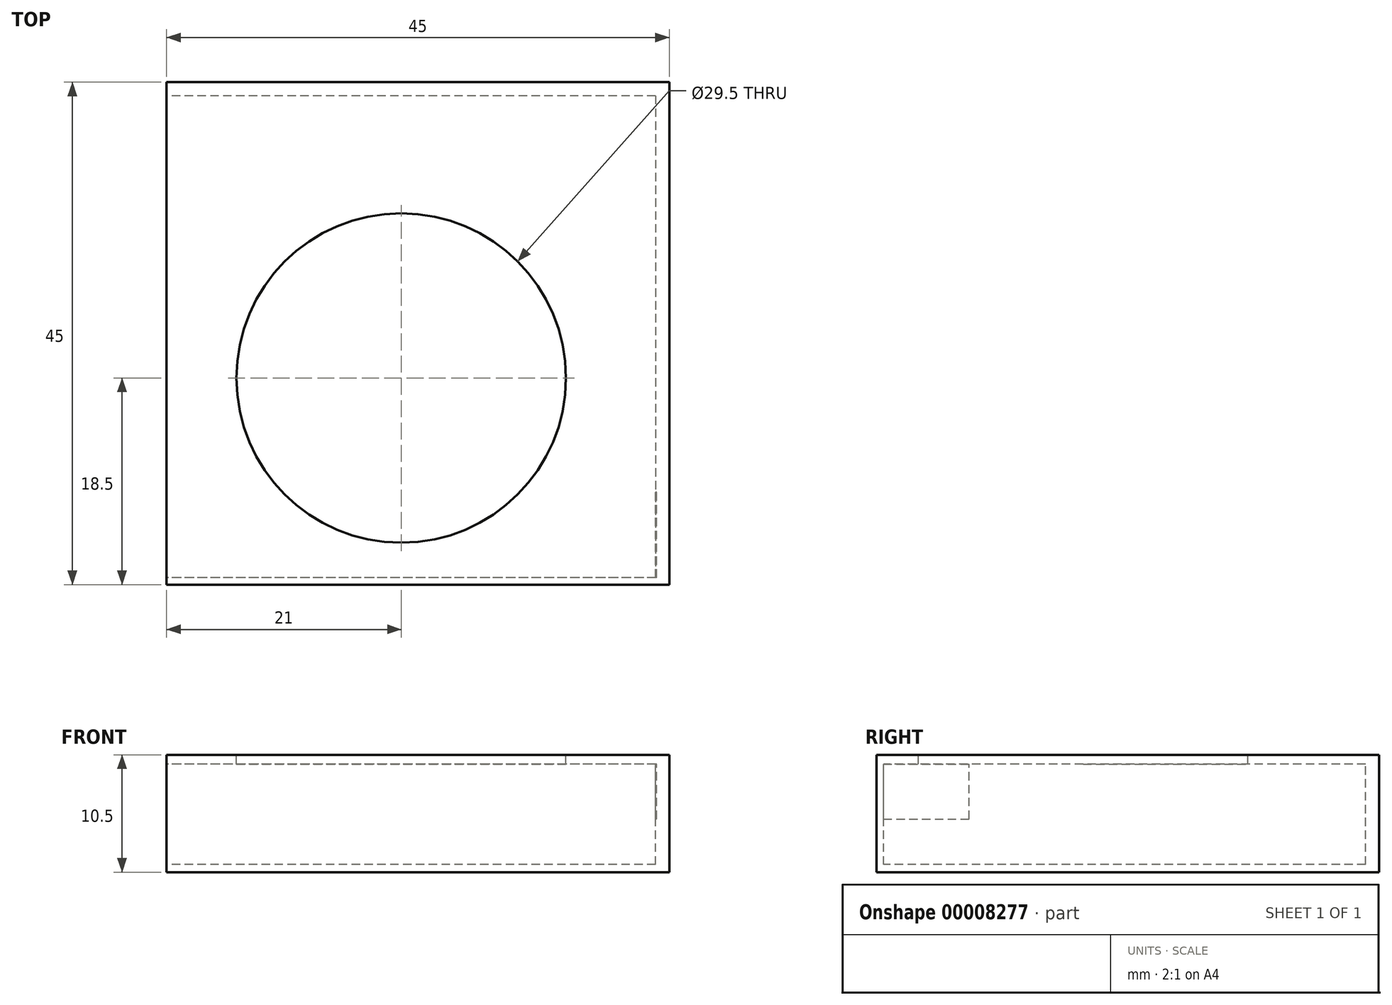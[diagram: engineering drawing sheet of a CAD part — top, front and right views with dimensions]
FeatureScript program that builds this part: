
annotation { "Feature Type Name" : "Feature", "Feature Type Description" : "" }
export const myFeature = defineFeature(function(context is Context, id is Id, definition is map)
    precondition{}
    {
        {
            var Q0;
            Q0=qCreatedBy(makeId("Top.planeOp"),FACE);
            var sketch = newSketch(context, id + "F0", { "sketchPlane" : qUnion([Q0])});
            skLineSegment(sketch, "E0.rect.bottom", {"start": v(-22.5, 22.5) * mm, "end": v(22.5, 22.5) * mm});
            skLineSegment(sketch, "E0.rect.top", {"start": v(-22.5, -22.5) * mm, "end": v(22.5, -22.5) * mm});
            skLineSegment(sketch, "E0.rect.left", {"start": v(-22.5, 22.5) * mm, "end": v(-22.5, -22.5) * mm});
            skLineSegment(sketch, "E0.rect.right", {"start": v(22.5, 22.5) * mm, "end": v(22.5, -22.5) * mm});
            skPoint(sketch, "E0.rect.middle", {"position": v(0, 0) * mm});
            skSolve(sketch);
        }
        {
            var Q0;
            Q0=makeQuery(id+"F0.imprint","IMPRINT",FACE,{"disambiguationData":[TD([[makeQuery(id+"F0.imprint","IMPRINT",EDGE,{"derivedFrom":sQuery(id+"F0.wireOp",EDGE,"E0.rect.bottom")}),-1.0]])]});
            extrude(context, id + "F1", {"entities" : qUnion([Q0]), "depth" : 10.5 * mm});
        }
        {
            var Q0;
            Q0=makeQuery(id+"F1.opExtrude","CAP_FACE",FACE,{"disambiguationData":[OSD([sQuery(id+"F0.wireOp",EDGE,"E0.rect.bottom"),sQuery(id+"F0.wireOp",EDGE,"E0.rect.top"),sQuery(id+"F0.wireOp",EDGE,"E0.rect.left"),sQuery(id+"F0.wireOp",EDGE,"E0.rect.right")])],"isStart":false});
            var sketch = newSketch(context, id + "F2", { "sketchPlane" : qUnion([Q0])});
            skCircle(sketch, "E1", {"center": v(-1.5, -4) * mm, "radius": 14.75 * mm});
            skSolve(sketch);
        }
        {
            var Q0;
            Q0 = qSketchRegion(id + "F2", true);
            extrude(context, id + "F3", {"entities" : qUnion([Q0]), "operationType" : NewBodyOperationType.REMOVE, "endBound" : BoundingType.SYMMETRIC, "oppositeDirection" : true, "depth" : 11.48 * mm});
        }
        {
            var Q0;
            Q0=makeQuery(id+"F1.opExtrude","SWEPT_FACE",FACE,{"disambiguationData":[OSD([sQuery(id+"F0.wireOp",EDGE,"E0.rect.left")])]});
            var sketch = newSketch(context, id + "F4", { "sketchPlane" : qUnion([Q0])});
            skLineSegment(sketch, "E2.left", {"start": v(-495.71, -51.1) * mm, "end": v(-495.71, 61.54) * mm});
            skLineSegment(sketch, "E3.bottom", {"start": v(-21.28, 0.67) * mm, "end": v(14.22, 0.67) * mm});
            skLineSegment(sketch, "E3.top", {"start": v(-21.28, 9.67) * mm, "end": v(14.22, 9.67) * mm});
            skLineSegment(sketch, "E3.left", {"start": v(-21.28, 0.67) * mm, "end": v(-21.28, 9.67) * mm});
            skLineSegment(sketch, "E3.right", {"start": v(14.22, 0.67) * mm, "end": v(14.22, 9.67) * mm});
            skSolve(sketch);
        }
        {
            var Q0;
            Q0=makeQuery(id+"F4.imprint","IMPRINT",FACE,{"disambiguationData":[TD([[makeQuery(id+"F4.imprint","IMPRINT",EDGE,{"derivedFrom":sQuery(id+"F4.wireOp",EDGE,"E3.bottom")}),1.0]])]});
            extrude(context, id + "F5", {"entities" : qUnion([Q0]), "operationType" : NewBodyOperationType.REMOVE, "oppositeDirection" : true, "depth" : 43.76 * mm});
        }
        {
            var Q0;
            Q0=makeQuery(id+"F5.boolean.opBoolean","COPY",FACE,{"derivedFrom":makeQuery(id+"F5.opExtrude","SWEPT_FACE",FACE,{"disambiguationData":[OSD([sQuery(id+"F4.wireOp",EDGE,"E3.right")])]})});
            extrude(context, id + "F6", {"entities" : qUnion([Q0]), "operationType" : NewBodyOperationType.REMOVE, "oppositeDirection" : true, "depth" : 7.66 * mm});
        }
        {
            var Q0;
            {var subQ0=sQuery(id+"F2.wireOp",EDGE,"E1");var subQ1=sQuery(id+"F4.wireOp",EDGE,"E3.right");Q0=makeQuery(id+"F6.boolean.opBoolean","COPY",FACE,{"derivedFrom":makeQuery(id+"F6.opExtrude","SWEPT_FACE",FACE,{"disambiguationData":[OSD([subQ0,subQ1]),TDD([makeQuery(id+"F5.boolean.opBoolean","INTERSECT",EDGE,{"disambiguationData":[OD(0.0)],"derivedFrom":[makeQuery(id+"F3.boolean.opBoolean","COPY",FACE,{"derivedFrom":makeQuery(id+"F3.opExtrude","SWEPT_FACE",FACE,{"disambiguationData":[OSD([subQ0])]})}),makeQuery(id+"F5.opExtrude","SWEPT_FACE",FACE,{"disambiguationData":[OSD([subQ1])]})]})])]})});}
            extrude(context, id + "F7", {"entities" : qUnion([Q0]), "operationType" : NewBodyOperationType.REMOVE, "oppositeDirection" : true, "depth" : 33.52 * mm});
        }
    });
